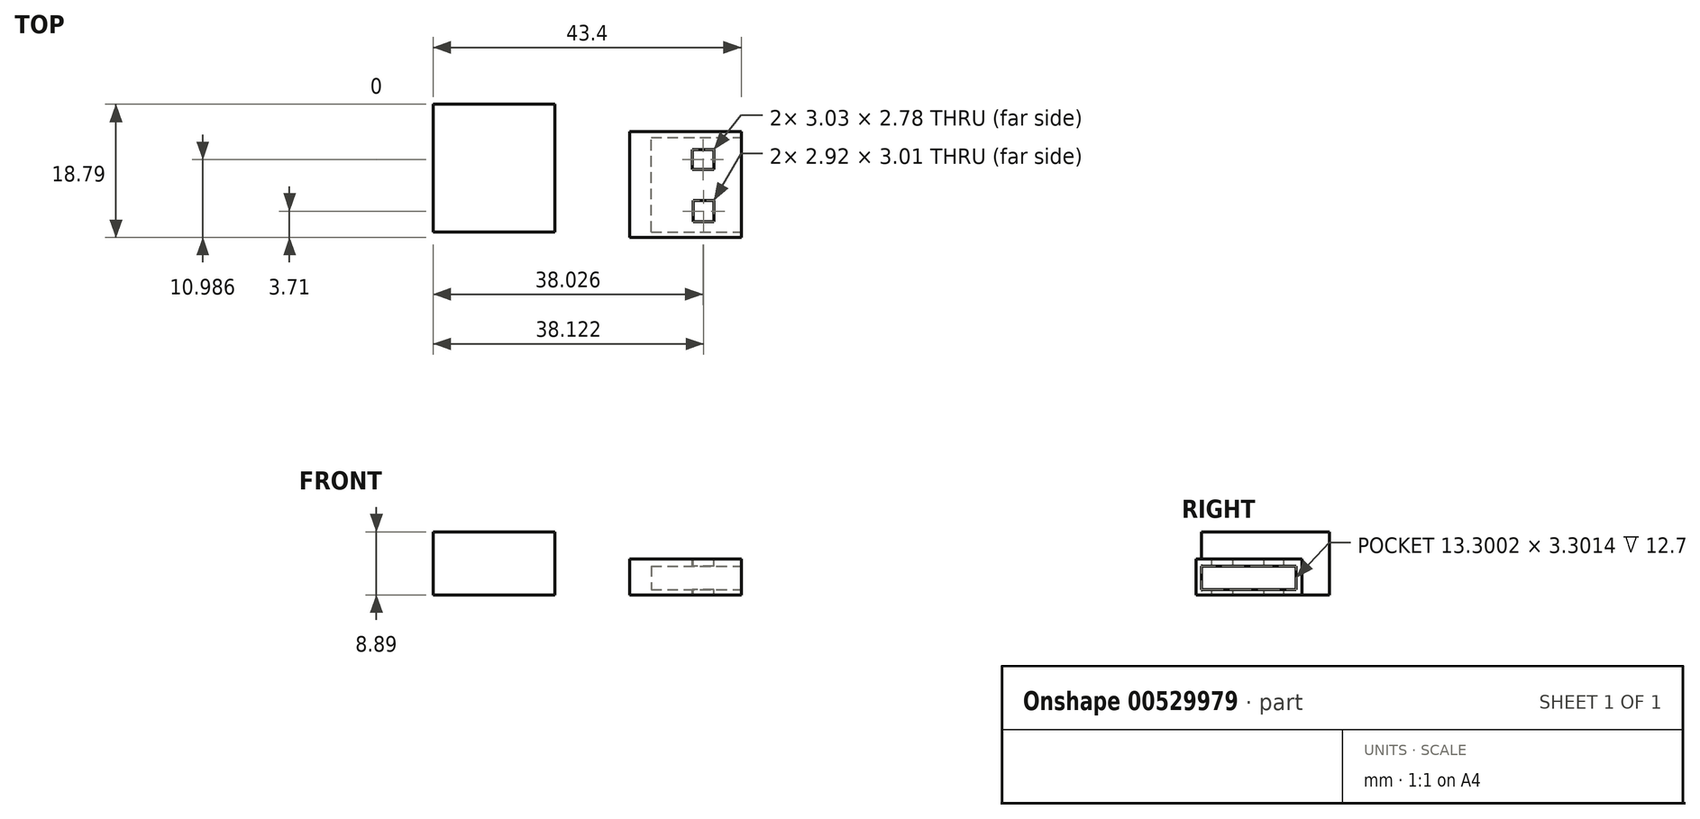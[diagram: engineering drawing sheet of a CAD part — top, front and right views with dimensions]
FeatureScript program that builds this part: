
annotation { "Feature Type Name" : "Feature", "Feature Type Description" : "" }
export const myFeature = defineFeature(function(context is Context, id is Id, definition is map)
    precondition{}
    {
        {
            var Q0;
            Q0=qCreatedBy(makeId("Top.planeOp"),FACE);
            var sketch = newSketch(context, id + "F0", { "sketchPlane" : qUnion([Q0])});
            skLineSegment(sketch, "E0.bottom", {"start": v(-59.64, 47.24) * mm, "end": v(-42.51, 47.24) * mm});
            skLineSegment(sketch, "E0.top", {"start": v(-59.64, 29.23) * mm, "end": v(-42.51, 29.23) * mm});
            skLineSegment(sketch, "E0.left", {"start": v(-59.64, 47.24) * mm, "end": v(-59.64, 29.23) * mm});
            skLineSegment(sketch, "E0.right", {"start": v(-42.51, 47.24) * mm, "end": v(-42.51, 29.23) * mm});
            skSolve(sketch);
        }
        {
            var Q0;
            Q0=makeQuery(id+"F0.imprint","IMPRINT",FACE,{"disambiguationData":[TD([[makeQuery(id+"F0.imprint","IMPRINT",EDGE,{"derivedFrom":sQuery(id+"F0.wireOp",EDGE,"E0.bottom")}),-1.0]])]});
            extrude(context, id + "F1", {"entities" : qUnion([Q0]), "depth" : 8.9 * mm, "offsetDistance" : 25.4 * mm});
        }
        {
            var Q0;
            Q0=qCreatedBy(makeId("Top.planeOp"),FACE);
            var sketch = newSketch(context, id + "F2", { "sketchPlane" : qUnion([Q0])});
            skLineSegment(sketch, "E1.bottom", {"start": v(-31.98, 43.4) * mm, "end": v(-16.24, 43.4) * mm});
            skLineSegment(sketch, "E1.top", {"start": v(-31.98, 28.45) * mm, "end": v(-16.24, 28.45) * mm});
            skLineSegment(sketch, "E1.left", {"start": v(-31.98, 43.4) * mm, "end": v(-31.98, 28.45) * mm});
            skLineSegment(sketch, "E1.right", {"start": v(-16.24, 43.4) * mm, "end": v(-16.24, 28.45) * mm});
            skSolve(sketch);
        }
        {
            var Q0;
            Q0=makeQuery(id+"F2.imprint","IMPRINT",FACE,{"disambiguationData":[TD([[makeQuery(id+"F2.imprint","IMPRINT",EDGE,{"derivedFrom":sQuery(id+"F2.wireOp",EDGE,"E1.bottom")}),-1.0]])]});
            extrude(context, id + "F3", {"entities" : qUnion([Q0]), "depth" : 5.08 * mm, "offsetDistance" : 25.4 * mm});
        }
        {
            var Q0;
            Q0=makeQuery(id+"F3.opExtrude","SWEPT_FACE",FACE,{"disambiguationData":[OSD([sQuery(id+"F2.wireOp",EDGE,"E1.right")])]});
            var sketch = newSketch(context, id + "F4", { "sketchPlane" : qUnion([Q0])});
            skLineSegment(sketch, "E2.bottom", {"start": v(29.24, 4.07) * mm, "end": v(42.54, 4.07) * mm});
            skLineSegment(sketch, "E2.top", {"start": v(29.24, 0.77) * mm, "end": v(42.54, 0.77) * mm});
            skLineSegment(sketch, "E2.left", {"start": v(29.24, 4.07) * mm, "end": v(29.24, 0.77) * mm});
            skLineSegment(sketch, "E2.right", {"start": v(42.54, 4.07) * mm, "end": v(42.54, 0.77) * mm});
            skSolve(sketch);
        }
        {
            var Q0;
            Q0=makeQuery(id+"F4.imprint","IMPRINT",FACE,{"disambiguationData":[TD([[makeQuery(id+"F4.imprint","IMPRINT",EDGE,{"derivedFrom":sQuery(id+"F4.wireOp",EDGE,"E2.bottom")}),-1.0]])]});
            extrude(context, id + "F5", {"entities" : qUnion([Q0]), "operationType" : NewBodyOperationType.REMOVE, "oppositeDirection" : true, "depth" : 12.7 * mm, "offsetDistance" : 25.4 * mm});
        }
        {
            var Q0;
            Q0=makeQuery(id+"F3.opExtrude","CAP_FACE",FACE,{"disambiguationData":[OSD([sQuery(id+"F2.wireOp",EDGE,"E1.bottom"),sQuery(id+"F2.wireOp",EDGE,"E1.top"),sQuery(id+"F2.wireOp",EDGE,"E1.left"),sQuery(id+"F2.wireOp",EDGE,"E1.right")])],"isStart":false});
            var sketch = newSketch(context, id + "F6", { "sketchPlane" : qUnion([Q0])});
            skLineSegment(sketch, "E3.bottom", {"start": v(-23.13, 40.83) * mm, "end": v(-20.1, 40.83) * mm});
            skLineSegment(sketch, "E3.top", {"start": v(-23.13, 38.05) * mm, "end": v(-20.1, 38.05) * mm});
            skLineSegment(sketch, "E3.left", {"start": v(-23.13, 40.83) * mm, "end": v(-23.13, 38.05) * mm});
            skLineSegment(sketch, "E3.right", {"start": v(-20.1, 40.83) * mm, "end": v(-20.1, 38.05) * mm});
            skLineSegment(sketch, "E4.bottom", {"start": v(-23.13, 34) * mm, "end": v(-20.1, 34) * mm});
            skLineSegment(sketch, "E4.top", {"start": v(-23.13, 30.97) * mm, "end": v(-20.1, 30.97) * mm});
            skLineSegment(sketch, "E4.left", {"start": v(-23.13, 34) * mm, "end": v(-23.13, 30.97) * mm});
            skLineSegment(sketch, "E4.right", {"start": v(-20.1, 34) * mm, "end": v(-20.1, 30.97) * mm});
            skSolve(sketch);
        }
        {
            var Q0;
            Q0=makeQuery(id+"F6.imprint","IMPRINT",FACE,{"disambiguationData":[TD([[makeQuery(id+"F6.imprint","IMPRINT",EDGE,{"derivedFrom":sQuery(id+"F6.wireOp",EDGE,"E3.bottom")}),-1.0]])]});
            extrude(context, id + "F7", {"entities" : qUnion([Q0]), "operationType" : NewBodyOperationType.REMOVE, "oppositeDirection" : true, "depth" : 25.4 * mm, "offsetDistance" : 25.4 * mm});
        }
        {
            var Q0;
            Q0=makeQuery(id+"F3.opExtrude","CAP_FACE",FACE,{"disambiguationData":[OSD([sQuery(id+"F2.wireOp",EDGE,"E1.bottom"),sQuery(id+"F2.wireOp",EDGE,"E1.top"),sQuery(id+"F2.wireOp",EDGE,"E1.left"),sQuery(id+"F2.wireOp",EDGE,"E1.right")])],"isStart":false});
            var sketch = newSketch(context, id + "F8", { "sketchPlane" : qUnion([Q0])});
            skLineSegment(sketch, "E5.bottom", {"start": v(-22.98, 33.67) * mm, "end": v(-20.06, 33.67) * mm});
            skLineSegment(sketch, "E5.top", {"start": v(-22.98, 30.65) * mm, "end": v(-20.06, 30.65) * mm});
            skLineSegment(sketch, "E5.left", {"start": v(-22.98, 33.67) * mm, "end": v(-22.98, 30.65) * mm});
            skLineSegment(sketch, "E5.right", {"start": v(-20.06, 33.67) * mm, "end": v(-20.06, 30.65) * mm});
            skSolve(sketch);
        }
        {
            var Q0;
            Q0=makeQuery(id+"F8.imprint","IMPRINT",FACE,{"disambiguationData":[TD([[makeQuery(id+"F8.imprint","IMPRINT",EDGE,{"derivedFrom":sQuery(id+"F8.wireOp",EDGE,"E5.bottom")}),-1.0]])]});
            extrude(context, id + "F9", {"entities" : qUnion([Q0]), "operationType" : NewBodyOperationType.REMOVE, "oppositeDirection" : true, "depth" : 25.4 * mm, "offsetDistance" : 25.4 * mm});
        }
    });
